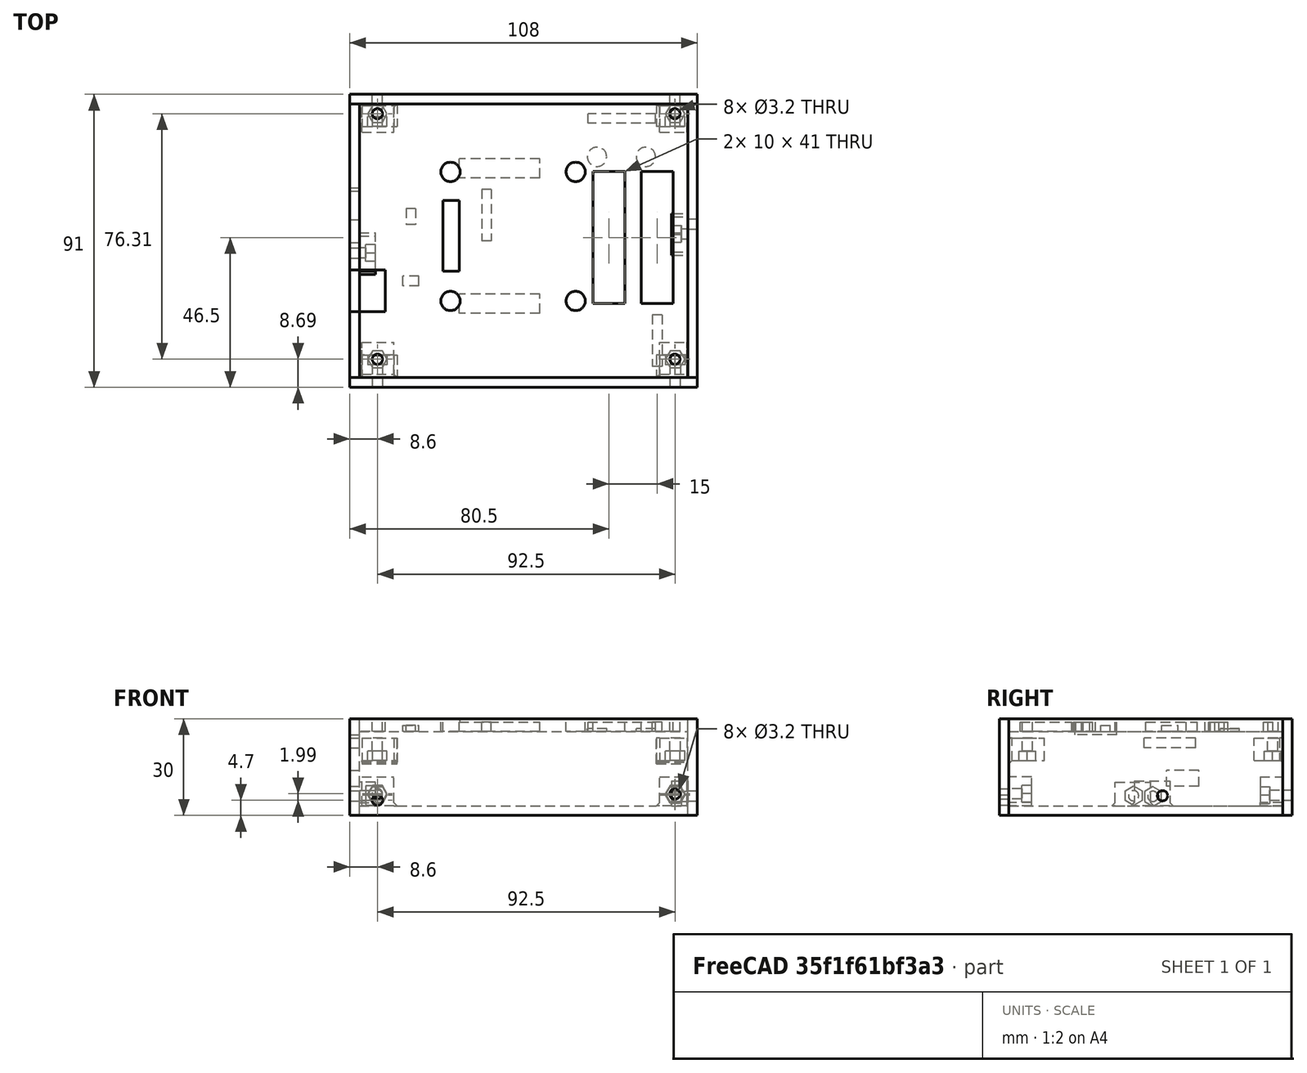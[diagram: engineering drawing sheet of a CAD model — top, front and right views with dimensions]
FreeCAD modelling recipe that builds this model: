
FCSTD DOCUMENT  (FreeCAD 0.16R6703 (Git))
Label: lightwand_box
License: All rights reserved
LicenseURL: http://en.wikipedia.org/wiki/All_rights_reserved
objects: Part::Cylinder×31, Part::Box×30, Part::Cut×30, Part::MultiFuse×11, Part::Prism×10, Part::Chamfer×5, Mesh::Feature×1
note: 117 computed .brp shape members not serialized (recipe doc carries the construction recipe); baked Part::Feature solids carry a one-line shape summary decoded from their .brp

FEATURE [Mesh::Feature] lightwand
FEATURE [Part::Box] Box  label="Cube_top"
  Height = 4
  Length = 102
  Placement = pos=(-2,0,1) rot=(0,0,1;0rad)
  Width = 85
FEATURE [Part::Box] Box001  label="Cube_bottom"
  Height = 3
  Length = 102
  Placement = pos=(-2,0,-25) rot=(0,0,1;0rad)
  Width = 85
FEATURE [Part::Box] Box002  label="Cube_front"
  Height = 30
  Length = 3
  Placement = pos=(-5,0,-25) rot=(0,0,1;0rad)
  Width = 85
FEATURE [Part::Box] Box003  label="Cube_back"
  Height = 30
  Length = 3
  Placement = pos=(100,0,-25) rot=(0,0,1;0rad)
  Width = 85
FEATURE [Part::Box] Box004  label="Cube_right"
  Height = 30
  Length = 108
  Placement = pos=(-5,-3,-25) rot=(0,0,1;0rad)
  Width = 3
FEATURE [Part::Box] Box005  label="Cube_left"
  Height = 30
  Length = 108
  Placement = pos=(-5,85,-25) rot=(0,0,1;0rad)
  Width = 3
FEATURE [Part::Box] Box006  label="led array connector"
  Height = 10
  Length = 17
  Placement = pos=(-11,20.5,0) rot=(0,0,1;0rad)
  Width = 13
FEATURE [Part::Box] Box007  label="led array connector001"
  Height = 10
  Length = 17
  Placement = pos=(-11,20.5,0) rot=(0,0,1;0rad)
  Width = 13
FEATURE [Part::Box] Box008  label="USB connector002"
  Height = 5
  Length = 17
  Placement = pos=(-11,49,-16) rot=(0,0,1;0rad)
  Width = 10
FEATURE [Part::Cut] Cut001  label="top without led array connector"
  Base = -> Box
  Tool = -> Box006
FEATURE [Part::Box] Box009  label="button array"
  Height = 10
  Length = 10
  Placement = pos=(70.5,23,0) rot=(0,0,1;0rad)
  Width = 41
FEATURE [Part::Box] Box010  label="button array001"
  Height = 10
  Length = 10
  Placement = pos=(85.5,23,0) rot=(0,0,1;0rad)
  Width = 41
FEATURE [Part::MultiFuse] Fusion001  label="button arrays"
  Shapes = -> [Box010,Box009]
FEATURE [Part::Cut] Cut002
  Base = -> Cut001
  Tool = -> Fusion001
FEATURE [Part::Cylinder] Cylinder  label="screen hole 1"
  Angle = 360
  Height = 10
  Placement = pos=(26.3,23.81,0) rot=(0,0,1;0rad)
  Radius = 3
FEATURE [Part::Cylinder] Cylinder001  label="screen hole 002"
  Angle = 360
  Height = 10
  Placement = pos=(26.3,63.91,0) rot=(0,0,1;0rad)
  Radius = 3
FEATURE [Part::Cylinder] Cylinder002  label="screen hole 003"
  Angle = 360
  Height = 10
  Placement = pos=(65.19,23.81,0) rot=(0,0,1;0rad)
  Radius = 3
FEATURE [Part::Cylinder] Cylinder003  label="screen hole 004"
  Angle = 360
  Height = 10
  Placement = pos=(65.19,63.91,0) rot=(0,0,1;0rad)
  Radius = 3
FEATURE [Part::Box] Box011  label="screen_pin_connection"
  Height = 10
  Length = 5
  Placement = pos=(24,33,0) rot=(0,0,1;0rad)
  Width = 22
FEATURE [Part::MultiFuse] Fusion002  label="screen holes"
  Shapes = -> [Box011,Cylinder001,Cylinder002,Cylinder,Cylinder003]
FEATURE [Part::Cut] Cut003
  Base = -> Cut002
  Tool = -> Fusion002
FEATURE [Part::Box] Box012  label="pins_accelerometer"
  Height = 4
  Length = 21
  Placement = pos=(69,79,0) rot=(0,0,1;0rad)
  Width = 3
FEATURE [Part::Box] Box013  label="pins_bluetooth"
  Height = 4
  Length = 16
  Placement = pos=(92,3.5,0) rot=(0,0,1;1.5708rad)
  Width = 3
FEATURE [Part::Box] Box014  label="pins_sd card reader"
  Height = 4
  Length = 16
  Placement = pos=(39,42.5,0) rot=(0,0,1;1.5708rad)
  Width = 3
FEATURE [Part::Box] Box015  label="pins_TIVA 1"
  Height = 4
  Length = 25
  Placement = pos=(29,62,0) rot=(0,0,1;0rad)
  Width = 6
FEATURE [Part::Box] Box016  label="pins_TIVA 2"
  Height = 4
  Length = 25
  Placement = pos=(29,20,0) rot=(0,0,1;0rad)
  Width = 6
FEATURE [Part::Box] Box017  label="SMD resistor"
  Height = 3
  Length = 5
  Placement = pos=(11.5,28.5,0) rot=(0,0,1;0rad)
  Width = 3
FEATURE [Part::Box] Box018  label="SMD capacitor"
  Height = 3
  Length = 5
  Placement = pos=(15.5,47.5,0) rot=(0,0,1;1.5708rad)
  Width = 3
FEATURE [Part::Cylinder] Cylinder004  label="accelerometer screw 1"
  Angle = 360
  Height = 2
  Placement = pos=(86.99,68.6,0) rot=(0,0,1;0rad)
  Radius = 3
FEATURE [Part::Cylinder] Cylinder005  label="accelerometer screw 2"
  Angle = 360
  Height = 2
  Placement = pos=(71.83,68.6,0) rot=(0,0,1;0rad)
  Radius = 3
FEATURE [Part::Box] Box019  label="SD card reader"
  Height = 3
  Length = 6
  Placement = pos=(-8,42,-4) rot=(0,0,1;0rad)
  Width = 16
FEATURE [Part::MultiFuse] Fusion
  Shapes = -> [Box007,Box008,Box019]
FEATURE [Part::Cut] Cut  label="front"
  Base = -> Box002
  Tool = -> Fusion
FEATURE [Part::Cylinder] Cylinder006  label="board hole 1"
  Angle = 360
  Height = 10
  Placement = pos=(3.6,5.69,0) rot=(0,0,1;0rad)
  Radius = 1.6
FEATURE [Part::Cylinder] Cylinder007  label="board hole 2"
  Angle = 360
  Height = 10
  Placement = pos=(3.6,82,0) rot=(0,0,1;0rad)
  Radius = 1.6
FEATURE [Part::Cylinder] Cylinder008  label="board hole 3"
  Angle = 360
  Height = 10
  Placement = pos=(96,5.69,0) rot=(0,0,1;0rad)
  Radius = 1.6
FEATURE [Part::Cylinder] Cylinder009  label="board hole 4"
  Angle = 360
  Height = 10
  Placement = pos=(96,82,0) rot=(0,0,1;0rad)
  Radius = 1.6
FEATURE [Part::MultiFuse] Fusion004  label="board holes"
  Shapes = -> [Cylinder006,Cylinder008,Cylinder007,Cylinder009]
FEATURE [Part::MultiFuse] Fusion003  label="pins, SMDs and holes"
  Shapes = -> [Box012,Box014,Box018,Box013,Box015,Box016,Box017,Cylinder004,Cylinder005,Fusion004]
FEATURE [Part::Cylinder] Cylinder010  label="board hole 005"
  Angle = 360
  Height = 10
  Placement = pos=(3.6,5.69,0) rot=(0,0,1;0rad)
  Radius = 1.6
FEATURE [Part::Cylinder] Cylinder011  label="board hole 006"
  Angle = 360
  Height = 10
  Placement = pos=(3.6,82,0) rot=(0,0,1;0rad)
  Radius = 1.6
FEATURE [Part::Cylinder] Cylinder012  label="board hole 007"
  Angle = 360
  Height = 10
  Placement = pos=(96,5.69,0) rot=(0,0,1;0rad)
  Radius = 1.6
FEATURE [Part::Cylinder] Cylinder013  label="board hole 008"
  Angle = 360
  Height = 10
  Placement = pos=(96,82,0) rot=(0,0,1;0rad)
  Radius = 1.6
FEATURE [Part::MultiFuse] Fusion005  label="pins_SMDs and holes"
  Shapes = -> [Fusion003,Cylinder010,Cylinder012,Cylinder011,Cylinder013]
FEATURE [Part::Cut] Cut004  label="final top"
  Base = -> Cut003
  Tool = -> Fusion005
FEATURE [Part::Cylinder] Cylinder014  label="board hole 009"
  Angle = 360
  Height = 16
  Placement = pos=(3.6,5.69,-20.3) rot=(1,0,0;1.5708rad)
  Radius = 1.6
FEATURE [Part::Cylinder] Cylinder015  label="left hole 1"
  Angle = 360
  Height = 10
  Placement = pos=(3.6,82,-18.7) rot=(-1,0,0;1.5708rad)
  Radius = 1.6
FEATURE [Part::Cylinder] Cylinder016  label="board hole 011"
  Angle = 360
  Height = 10
  Placement = pos=(96,5.69,-18.4) rot=(1,0,0;1.5708rad)
  Radius = 1.6
FEATURE [Part::Cylinder] Cylinder017  label="left hole 2"
  Angle = 360
  Height = 10
  Placement = pos=(96,82,-18.7) rot=(-1,0,0;1.5708rad)
  Radius = 1.6
FEATURE [Part::Box] Box020  label="Cube"
  Height = 7
  Length = 10
  Placement = pos=(-1.25,0,-7) rot=(0,0,1;0rad)
  Width = 11
FEATURE [Part::Prism] Prism
  Circumradius = 3
  Height = 3
  Placement = pos=(3.6,5.69,-7) rot=(0,0,1;0rad)
  Polygon = 6
FEATURE [Part::Cut] Cut005
  Base = -> Box020
  Placement = pos=(0,0,-1) rot=(0,0,1;0rad)
  Tool = -> Prism
FEATURE [Part::Cut] Cut006  label="nut to board right 1"
  Base = -> Cut005
  Tool = -> Cylinder014
FEATURE [Part::Cylinder] Cylinder018  label="board hole 013"
  Angle = 360
  Height = 12
  Placement = pos=(3.6,5.69,-7) rot=(0,0,1;0rad)
  Radius = 1.6
FEATURE [Part::Box] Box021  label="Cube001"
  Height = 7
  Length = 8.5
  Placement = pos=(-1.25,0,-7) rot=(0,0,1;0rad)
  Width = 11
FEATURE [Part::Prism] Prism001
  Circumradius = 3
  Height = 3
  Placement = pos=(3.6,5.69,-7) rot=(0,0,1;0rad)
  Polygon = 6
FEATURE [Part::Cut] Cut007
  Base = -> Box021
  Placement = pos=(0,0,-1) rot=(0,0,1;0rad)
  Tool = -> Prism001
FEATURE [Part::Cut] Cut008  label="nut to board right 2"
  Base = -> Cut007
  Placement = pos=(92.5,0,0) rot=(0,0,1;0rad)
  Tool = -> Cylinder018
FEATURE [Part::Cylinder] Cylinder019  label="board hole 014"
  Angle = 360
  Height = 10
  Placement = pos=(3.6,5.69,-5) rot=(0,0,1;0rad)
  Radius = 1.6
FEATURE [Part::Box] Box022  label="Cube002"
  Height = 7
  Length = 10
  Placement = pos=(-1.25,0,-7) rot=(0,0,1;0rad)
  Width = 11
FEATURE [Part::Prism] Prism002
  Circumradius = 3
  Height = 3
  Placement = pos=(3.6,5.69,-7) rot=(0,0,1;0rad)
  Polygon = 6
FEATURE [Part::Cut] Cut009
  Base = -> Box022
  Placement = pos=(0,0,-1) rot=(0,0,1;0rad)
  Tool = -> Prism002
FEATURE [Part::Cut] Cut010  label="nut to board left 1"
  Base = -> Cut009
  Placement = pos=(0,76.2,0) rot=(0,0,1;0rad)
  Tool = -> Cylinder019
FEATURE [Part::Cylinder] Cylinder020  label="board hole 015"
  Angle = 360
  Height = 10
  Placement = pos=(3.6,5.69,-5) rot=(0,0,1;0rad)
  Radius = 1.6
FEATURE [Part::Box] Box023  label="Cube003"
  Height = 7
  Length = 8.5
  Placement = pos=(-1.25,0,-7) rot=(0,0,1;0rad)
  Width = 11
FEATURE [Part::Prism] Prism003
  Circumradius = 3
  Height = 3
  Placement = pos=(3.6,5.69,-7) rot=(0,0,1;0rad)
  Polygon = 6
FEATURE [Part::Cut] Cut011
  Base = -> Box023
  Placement = pos=(0,0,-1) rot=(0,0,1;0rad)
  Tool = -> Prism003
FEATURE [Part::Cut] Cut012  label="nut to board left 2"
  Base = -> Cut011
  Placement = pos=(92.5,76.2,0) rot=(0,0,1;0rad)
  Tool = -> Cylinder020
FEATURE [Part::Cylinder] Cylinder021  label="board hole 016"
  Angle = 360
  Height = 10
  Placement = pos=(3.6,5.69,-5) rot=(0,0,1;0rad)
  Radius = 1.6
FEATURE [Part::Box] Box024  label="Cube004"
  Height = 7
  Length = 8.5
  Placement = pos=(-1.25,0,-7) rot=(0,0,1;0rad)
  Width = 11
FEATURE [Part::Prism] Prism004
  Circumradius = 3
  Height = 3
  Placement = pos=(3.6,5.69,-7) rot=(0,0,1;0rad)
  Polygon = 6
FEATURE [Part::Cut] Cut013
  Base = -> Box024
  Placement = pos=(0,0,-1) rot=(0,0,1;0rad)
  Tool = -> Prism004
FEATURE [Part::Cut] Cut014  label="nut to board left 3"
  Base = -> Cut013
  Placement = pos=(92.5,86,-13) rot=(-1,0,0;1.5708rad)
  Tool = -> Cylinder021
FEATURE [Part::Cylinder] Cylinder022  label="board hole 017"
  Angle = 360
  Height = 10
  Placement = pos=(3.6,5.69,-5) rot=(0,0,1;0rad)
  Radius = 1.6
FEATURE [Part::Box] Box025  label="Cube005"
  Height = 7
  Length = 10
  Placement = pos=(-1.25,0,-7) rot=(0,0,1;0rad)
  Width = 11
FEATURE [Part::Prism] Prism005
  Circumradius = 3
  Height = 3
  Placement = pos=(3.6,5.69,-7) rot=(0,0,1;0rad)
  Polygon = 6
FEATURE [Part::Cut] Cut015
  Base = -> Box025
  Placement = pos=(0,0,-1) rot=(0,0,1;0rad)
  Tool = -> Prism005
FEATURE [Part::Cut] Cut016  label="nut to board left 4"
  Base = -> Cut015
  Placement = pos=(0,86,-13) rot=(-1,0,0;1.5708rad)
  Tool = -> Cylinder022
FEATURE [Part::Cylinder] Cylinder023  label="board hole 018"
  Angle = 360
  Height = 10
  Placement = pos=(3.6,5.69,-5) rot=(0,0,1;0rad)
  Radius = 1.6
FEATURE [Part::Box] Box026  label="Cube006"
  Height = 7
  Length = 8.5
  Placement = pos=(-1.25,0,-7) rot=(0,0,1;0rad)
  Width = 11
FEATURE [Part::Prism] Prism006
  Circumradius = 3
  Height = 3
  Placement = pos=(3.6,5.69,-7) rot=(0,0,1;0rad)
  Polygon = 6
FEATURE [Part::Cut] Cut017
  Base = -> Box026
  Placement = pos=(0,0,-1) rot=(0,0,1;0rad)
  Tool = -> Prism006
FEATURE [Part::Cut] Cut018  label="nut to board right 3"
  Base = -> Cut017
  Placement = pos=(92.5,-1,-24) rot=(1,0,0;1.5708rad)
  Tool = -> Cylinder023
FEATURE [Part::Cylinder] Cylinder024  label="board hole 019"
  Angle = 360
  Height = 10
  Placement = pos=(3.6,5.69,-5) rot=(0,0,1;0rad)
  Radius = 1.6
FEATURE [Part::Box] Box027  label="Cube007"
  Height = 7
  Length = 10
  Placement = pos=(-1.25,0,-7) rot=(0,0,1;0rad)
  Width = 11
FEATURE [Part::Prism] Prism007
  Circumradius = 3
  Height = 3
  Placement = pos=(3.6,5.69,-7) rot=(0,0,1;0rad)
  Polygon = 6
FEATURE [Part::Cut] Cut019
  Base = -> Box027
  Placement = pos=(0,0,-1) rot=(0,0,1;0rad)
  Tool = -> Prism007
FEATURE [Part::Cut] Cut020  label="nut to board right 4"
  Base = -> Cut019
  Placement = pos=(0,-1,-24) rot=(1,0,0;1.5708rad)
  Tool = -> Cylinder024
FEATURE [Part::Cylinder] Cylinder025  label="board hole 020"
  Angle = 360
  Height = 10
  Placement = pos=(3.6,5.69,-5) rot=(0,0,1;0rad)
  Radius = 1.6
FEATURE [Part::Box] Box028  label="Cube008"
  Height = 5
  Length = 9
  Placement = pos=(-1.25,0,-7) rot=(0,0,1;0rad)
  Width = 11
FEATURE [Part::Prism] Prism008
  Circumradius = 3
  Height = 3
  Placement = pos=(3.6,5.69,-7) rot=(0,0,1;0rad)
  Polygon = 6
FEATURE [Part::Cut] Cut021
  Base = -> Box028
  Placement = pos=(0,0,-1) rot=(0,0,1;0rad)
  Tool = -> Prism008
FEATURE [Part::Cut] Cut022  label="nut to front"
  Base = -> Cut021
  Placement = pos=(-5,33,-22.5) rot=(0,-1,0;1.5708rad)
  Tool = -> Cylinder025
FEATURE [Part::Cylinder] Cylinder026  label="front hole"
  Angle = 360
  Height = 10
  Placement = pos=(-7.4,38.69,-18.9) rot=(0,1,0;1.5708rad)
  Radius = 1.6
FEATURE [Part::Cylinder] Cylinder027  label="board hole 022"
  Angle = 360
  Height = 10
  Placement = pos=(3.6,5.69,-5) rot=(0,0,1;0rad)
  Radius = 1.6
FEATURE [Part::Box] Box029  label="Cube009"
  Height = 5
  Length = 9
  Placement = pos=(-1.25,0,-7) rot=(0,0,1;0rad)
  Width = 11
FEATURE [Part::Prism] Prism009
  Circumradius = 3
  Height = 3
  Placement = pos=(3.6,5.69,-7) rot=(0,0,1;0rad)
  Polygon = 6
FEATURE [Part::Cut] Cut023
  Base = -> Box029
  Placement = pos=(0,0,-1) rot=(0,0,1;0rad)
  Tool = -> Prism009
FEATURE [Part::Cut] Cut024  label="nut to back"
  Base = -> Cut023
  Placement = pos=(103,38,-14.5) rot=(0,1,0;1.5708rad)
  Tool = -> Cylinder027
FEATURE [Part::Cylinder] Cylinder028  label="back hole"
  Angle = 360
  Height = 10
  Placement = pos=(97.6,47.69,-18.9) rot=(0,1,0;1.5708rad)
  Radius = 1.6
FEATURE [Part::Cut] Cut025  label="final back"
  Base = -> Box003
  Tool = -> Cylinder028
FEATURE [Part::MultiFuse] Fusion006  label="left holes"
  Shapes = -> [Cylinder015,Cylinder017]
FEATURE [Part::Cut] Cut026  label="left side final"
  Base = -> Box005
  Tool = -> Fusion006
FEATURE [Part::Cut] Cut027  label="final front"
  Base = -> Cut
  Tool = -> Cylinder026
FEATURE [Part::MultiFuse] Fusion007  label="bottom with nut holders"
  Shapes = -> [Cut024,Cut022,Cut014,Cut016,Cut020,Cut018,Box001]
FEATURE [Part::Cylinder] Cylinder029  label="board hole 023"
  Angle = 360
  Height = 10
  Placement = pos=(3.6,5.69,-20.3) rot=(1,0,0;1.5708rad)
  Radius = 1.6
FEATURE [Part::MultiFuse] Fusion010
  Shapes = -> [Cylinder016,Cylinder029]
FEATURE [Part::Cut] Cut028  label="right with holes"
  Base = -> Box004
  Tool = -> Fusion010
FEATURE [Part::MultiFuse] Fusion011  label="right side"
  Shapes = -> [Cut006,Cut008,Cut028]
FEATURE [Part::MultiFuse] Fusion012  label="left side"
  Shapes = -> [Cut026,Cut010,Cut012]
FEATURE [Part::Chamfer] Chamfer  label="bottom"
  Base = -> Fusion007
  Edges = 8 edges r=1: [Edge2,Edge4,Edge9,Edge11,Edge16,Edge22,Edge27,Edge29]
FEATURE [Part::Chamfer] Chamfer001
  Base = -> Fusion012
  Edges = 2 edges r=1: [Edge12,Edge16]
FEATURE [Part::Chamfer] Chamfer002
  Base = -> Chamfer001
  Edges = 1 edges r=0.5: [Edge6]
FEATURE [Part::Chamfer] Chamfer003  label="left side final001"
  Base = -> Chamfer002
  Edges = 1 edges r=0.5: [Edge20]
FEATURE [Part::Chamfer] Chamfer004  label="right side001"
  Base = -> Fusion011
  Edges = 4 edges r=1: [Edge6,Edge19,Edge26,Edge27]
FEATURE [Part::Cylinder] Cylinder030  label="board hole 024"
  Angle = 360
  Height = 12
  Placement = pos=(3.6,5.69,-7) rot=(0,0,1;0rad)
  Radius = 1.6
FEATURE [Part::Cut] Cut029  label="right side final"
  Base = -> Chamfer004
  Tool = -> Cylinder030
